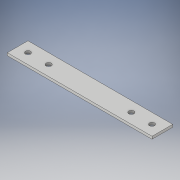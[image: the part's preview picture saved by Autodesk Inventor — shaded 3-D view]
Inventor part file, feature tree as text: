
AUTODESK INVENTOR PART (.ipt)
format: ipt  version: 2017 (Build 210142000, 142)  size: 106,496 bytes
history: native  units: in
note: dims shown in document units (in); Inventor stores cm internally (conversion verified against a paired STEP export)
features: extrude x2, sketch x2
ambient origin geometry x8: Origin, YZ Plane, XZ Plane, XY Plane, X Axis, Y Axis, Z Axis, Center Point
bodies: Solid1 (feature_tree)
feature tree (4):
  extrude  "Extrusion1"  Depth=1.0in
  extrude  "Extrusion2"  Depth=0.125in
  sketch  "Sketch1"  dims[d0=0.125in d1=1.0in]
  sketch  "Sketch2"  dims[d2=7.0in d3=0.0in d4=0.25in d5=2.0in d6=3.0in d7=0.125in d8=0.0in]
